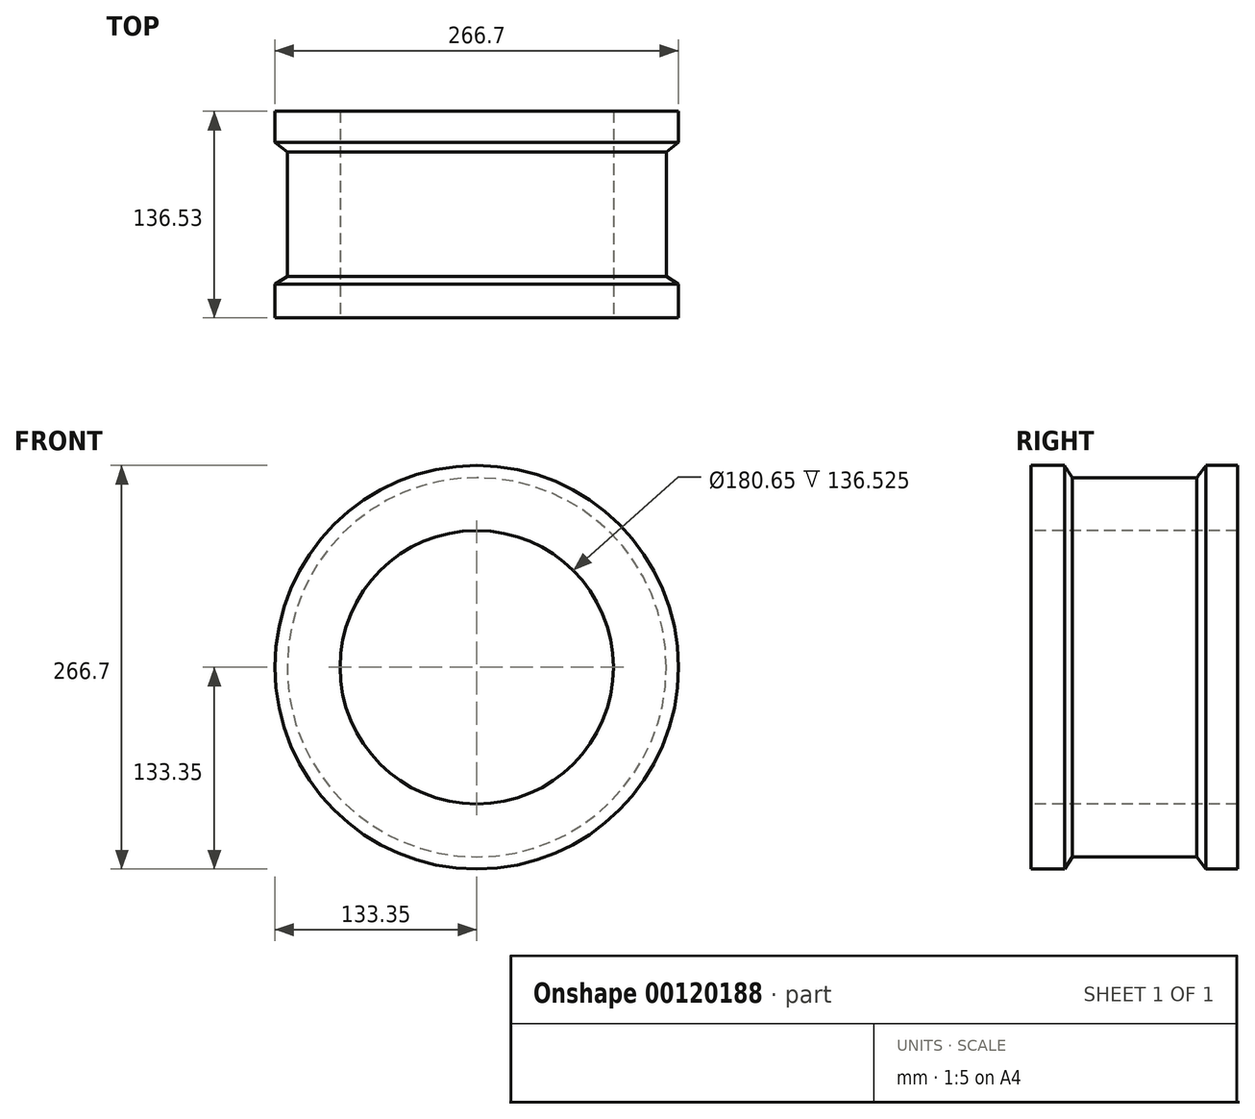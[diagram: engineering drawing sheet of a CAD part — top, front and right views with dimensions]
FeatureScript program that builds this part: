
annotation { "Feature Type Name" : "Feature", "Feature Type Description" : "" }
export const myFeature = defineFeature(function(context is Context, id is Id, definition is map)
    precondition{}
    {
        {
            var Q0;
            Q0=qCreatedBy(makeId("Right.planeOp"),FACE);
            var sketch = newSketch(context, id + "F0", { "sketchPlane" : qUnion([Q0])});
            skLineSegment(sketch, "E0", {"start": v(0, 0) * mm, "end": v(0, 133.35) * mm});
            skLineSegment(sketch, "E1", {"start": v(136.53, 133.35) * mm, "end": v(136.53, 0) * mm});
            skLineSegment(sketch, "E2", {"start": v(136.53, 0) * mm, "end": v(0, 0) * mm});
            skLineSegment(sketch, "E3", {"start": v(0, 133.35) * mm, "end": v(22.23, 133.35) * mm});
            skLineSegment(sketch, "E4", {"start": v(22.23, 133.35) * mm, "end": v(27.41, 125.27) * mm});
            skLineSegment(sketch, "E5", {"start": v(27.41, 125.27) * mm, "end": v(109.65, 125.27) * mm});
            skLineSegment(sketch, "E6", {"start": v(109.65, 125.27) * mm, "end": v(115.83, 133.35) * mm});
            skLineSegment(sketch, "E7", {"start": v(115.83, 133.35) * mm, "end": v(136.53, 133.35) * mm});
            skSolve(sketch);
        }
        {
            var Q0;
            Q0=makeQuery(id+"F0.imprint","IMPRINT",FACE,{"disambiguationData":[TD([[makeQuery(id+"F0.imprint","IMPRINT",EDGE,{"derivedFrom":sQuery(id+"F0.wireOp",EDGE,"E0")}),-1.0]])]});
            var Q1;
            Q1=sQuery(id+"F0.wireOp",EDGE,"E2");
            revolve(context, id + "F1", {"entities" : qUnion([Q0]), "axis" : qUnion([Q1]), "revolveType" : RevolveType.FULL});
        }
        {
            var Q0;
            Q0=makeQuery(id+"F1.opRevolve","SWEPT_FACE",FACE,{"disambiguationData":[OSD([sQuery(id+"F0.wireOp",EDGE,"E0")])]});
            var sketch = newSketch(context, id + "F2", { "sketchPlane" : qUnion([Q0])});
            skCircle(sketch, "E8", {"center": v(0, 0) * mm, "radius": 90.33 * mm});
            skSolve(sketch);
        }
        {
            var Q0;
            Q0 = qSketchRegion(id + "F2", true);
            extrude(context, id + "F3", {"entities" : qUnion([Q0]), "operationType" : NewBodyOperationType.REMOVE, "endBound" : BoundingType.THROUGH_ALL, "oppositeDirection" : true, "depth" : 25.4 * mm});
        }
    });
